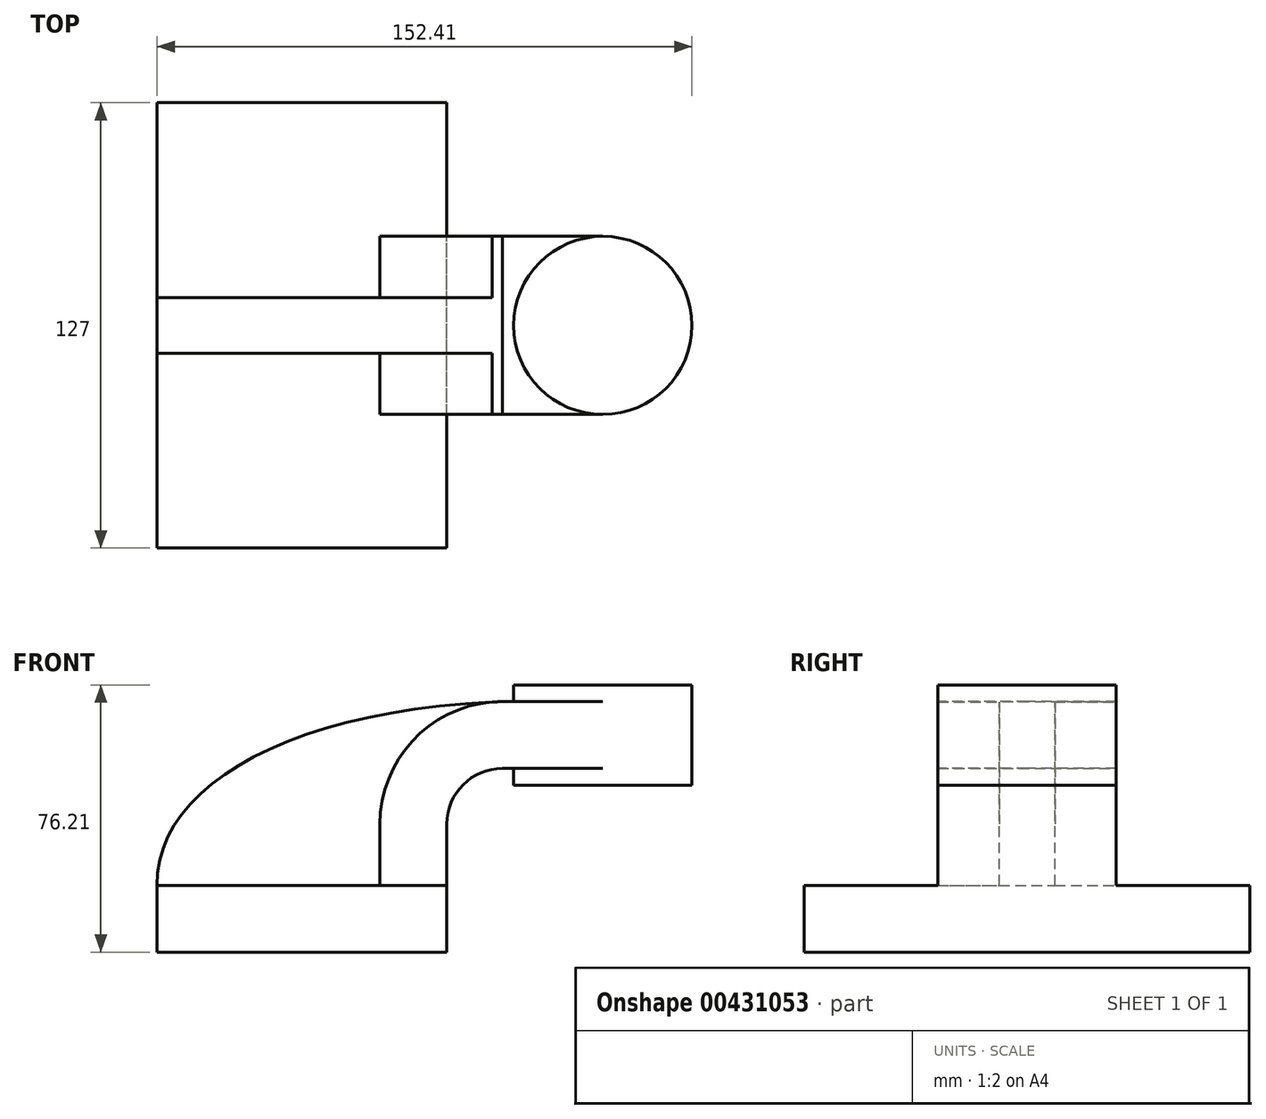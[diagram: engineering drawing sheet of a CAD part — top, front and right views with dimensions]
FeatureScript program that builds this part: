
annotation { "Feature Type Name" : "Feature", "Feature Type Description" : "" }
export const myFeature = defineFeature(function(context is Context, id is Id, definition is map)
    precondition{}
    {
        {
            var Q0;
            Q0=qCreatedBy(makeId("Front.planeOp"),FACE);
            var sketch = newSketch(context, id + "F0", { "sketchPlane" : qUnion([Q0])});
            skLineSegment(sketch, "E0.bottom", {"start": v(41.28, 9.53) * mm, "end": v(-41.28, 9.53) * mm});
            skLineSegment(sketch, "E0.top", {"start": v(41.28, -9.52) * mm, "end": v(-41.28, -9.52) * mm});
            skLineSegment(sketch, "E0.left", {"start": v(41.28, 9.53) * mm, "end": v(41.28, -9.52) * mm});
            skLineSegment(sketch, "E0.right", {"start": v(-41.28, 9.53) * mm, "end": v(-41.28, -9.52) * mm});
            skPoint(sketch, "E0.middle", {"position": v(0, 0) * mm});
            skLineSegment(sketch, "E1.bottom", {"start": v(111.12, 66.68) * mm, "end": v(60.33, 66.68) * mm});
            skLineSegment(sketch, "E1.top", {"start": v(111.12, 38.1) * mm, "end": v(60.33, 38.1) * mm});
            skLineSegment(sketch, "E1.left", {"start": v(111.12, 66.68) * mm, "end": v(111.12, 38.1) * mm});
            skLineSegment(sketch, "E1.right", {"start": v(60.32, 66.68) * mm, "end": v(60.33, 38.1) * mm});
            skPoint(sketch, "E1.middle", {"position": v(85.72, 52.39) * mm});
            skLineSegment(sketch, "E2", {"start": v(41.28, 9.53) * mm, "end": v(41.28, 26.99) * mm});
            skArc(sketch, "E3", {"start": v(41.27, 26.99) * mm, "mid": v(45.92, 38.21) * mm, "end": v(57.15, 42.86) * mm});
            skLineSegment(sketch, "E4", {"start": v(57.15, 42.86) * mm, "end": v(94.67, 42.86) * mm});
            skLineSegment(sketch, "E5.0", {"start": v(57.15, 61.91) * mm, "end": v(94.67, 61.91) * mm});
            skArc(sketch, "E5.1", {"start": v(22.22, 26.99) * mm, "mid": v(32.45, 51.68) * mm, "end": v(57.15, 61.91) * mm});
            skLineSegment(sketch, "E5.2", {"start": v(22.23, 9.53) * mm, "end": v(22.23, 26.99) * mm});
            skFitSpline(sketch, "E6", {"points": [v(-41.28, 9.53) * mm, v(57.15, 61.91) * mm], "startDerivative": vector(-1.35, 84.16) * mm, "endDerivative": vector(183.22, 6.85) * mm});
            skLineSegment(sketch, "E7", {"start": v(85.72, 38.1) * mm, "end": v(85.72, 66.68) * mm});
            skSolve(sketch);
        }
        {
            var Q0;
            Q0=makeQuery(id+"F0.imprint","IMPRINT",FACE,{"disambiguationData":[TD([[makeQuery(id+"F0.imprint","IMPRINT",EDGE,{"derivedFrom":sQuery(id+"F0.wireOp",EDGE,"E0.top")}),-1.0]])]});
            extrude(context, id + "F1", {"entities" : qUnion([Q0]), "endBound" : BoundingType.SYMMETRIC, "depth" : 127 * mm});
        }
        {
            var Q0;
            {var subQ1=sQuery(id+"F0.wireOp",EDGE,"E2");Q0=makeQuery(id+"F0.imprint","IMPRINT",FACE,{"disambiguationData":[TD([[makeQuery(id+"F0.imprint","IMPRINT",EDGE,{"derivedFrom":subQ1}),1.0]])]});}
            var Q1;
            {var subQ0=sQuery(id+"F0.wireOp",EDGE,"E5.0");var subQ1=sQuery(id+"F0.wireOp",EDGE,"E1.right");var subQ2=makeQuery(id+"F0.imprint","INTERSECT",VERTEX,{"derivedFrom":[subQ1,subQ0]});Q1=makeQuery(id+"F0.imprint","IMPRINT",FACE,{"disambiguationData":[TD([[makeQuery(id+"F0.imprint","IMPRINT",EDGE,{"disambiguationData":[TD([[subQ2,-1.0]])],"derivedFrom":subQ1}),1.0]])]});}
            extrude(context, id + "F2", {"entities" : qUnion([Q0, Q1]), "operationType" : NewBodyOperationType.ADD, "endBound" : BoundingType.SYMMETRIC, "depth" : 50.8 * mm});
        }
        {
            var Q0;
            {var subQ3=sQuery(id+"F0.wireOp",EDGE,"E5.2");Q0=makeQuery(id+"F0.imprint","IMPRINT",FACE,{"disambiguationData":[TD([[makeQuery(id+"F0.imprint","IMPRINT",EDGE,{"derivedFrom":subQ3}),1.0]])]});}
            extrude(context, id + "F3", {"entities" : qUnion([Q0]), "operationType" : NewBodyOperationType.ADD, "endBound" : BoundingType.SYMMETRIC, "depth" : 15.88 * mm});
        }
        {
            var Q0;
            {var subQ4=sQuery(id+"F0.wireOp",EDGE,"E1.left");Q0=makeQuery(id+"F0.imprint","IMPRINT",FACE,{"disambiguationData":[TD([[makeQuery(id+"F0.imprint","IMPRINT",EDGE,{"derivedFrom":subQ4}),-1.0]])]});}
            var Q1;
            Q1=sQuery(id+"F0.wireOp",EDGE,"E7");
            revolve(context, id + "F4", {"operationType" : NewBodyOperationType.ADD, "entities" : qUnion([Q0]), "axis" : qUnion([Q1]), "revolveType" : RevolveType.FULL});
        }
    });
